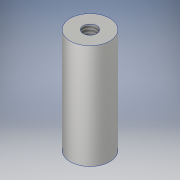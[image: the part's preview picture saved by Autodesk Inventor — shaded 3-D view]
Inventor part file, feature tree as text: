
AUTODESK INVENTOR PART (.ipt)
format: ipt  version: 2019 (Build 230136000, 136)  size: 101,888 bytes
history: native  units: in
note: dims shown in document units (in); Inventor stores cm internally (conversion verified against a paired STEP export)
features: sketch x2, extrude x1, hole x1
ambient origin geometry x8: Origin, YZ Plane, XZ Plane, XY Plane, X Axis, Y Axis, Z Axis, Center Point
bodies: Solid1 (feature_tree)
feature tree (4):
  extrude  "Extrusion1"  Depth=0.992in TaperAngle=0.0deg
  hole  "Hole1"  [1 undecoded]
  sketch  "Sketch1"  dims[d0=0.375in d1=0.992in d2=0.0in]
  sketch  "Sketch2"  dims[d3=0.13in d4=0.328in d5=0.332in d6=0.25in d7=0.5635in d8=1.0in d9=0.8108in]
note: 1 required parameter value undecoded (feature->parameter linkage not recoverable at this tier; creation-order binding heuristic only, values carry confidence <= 0.55)
